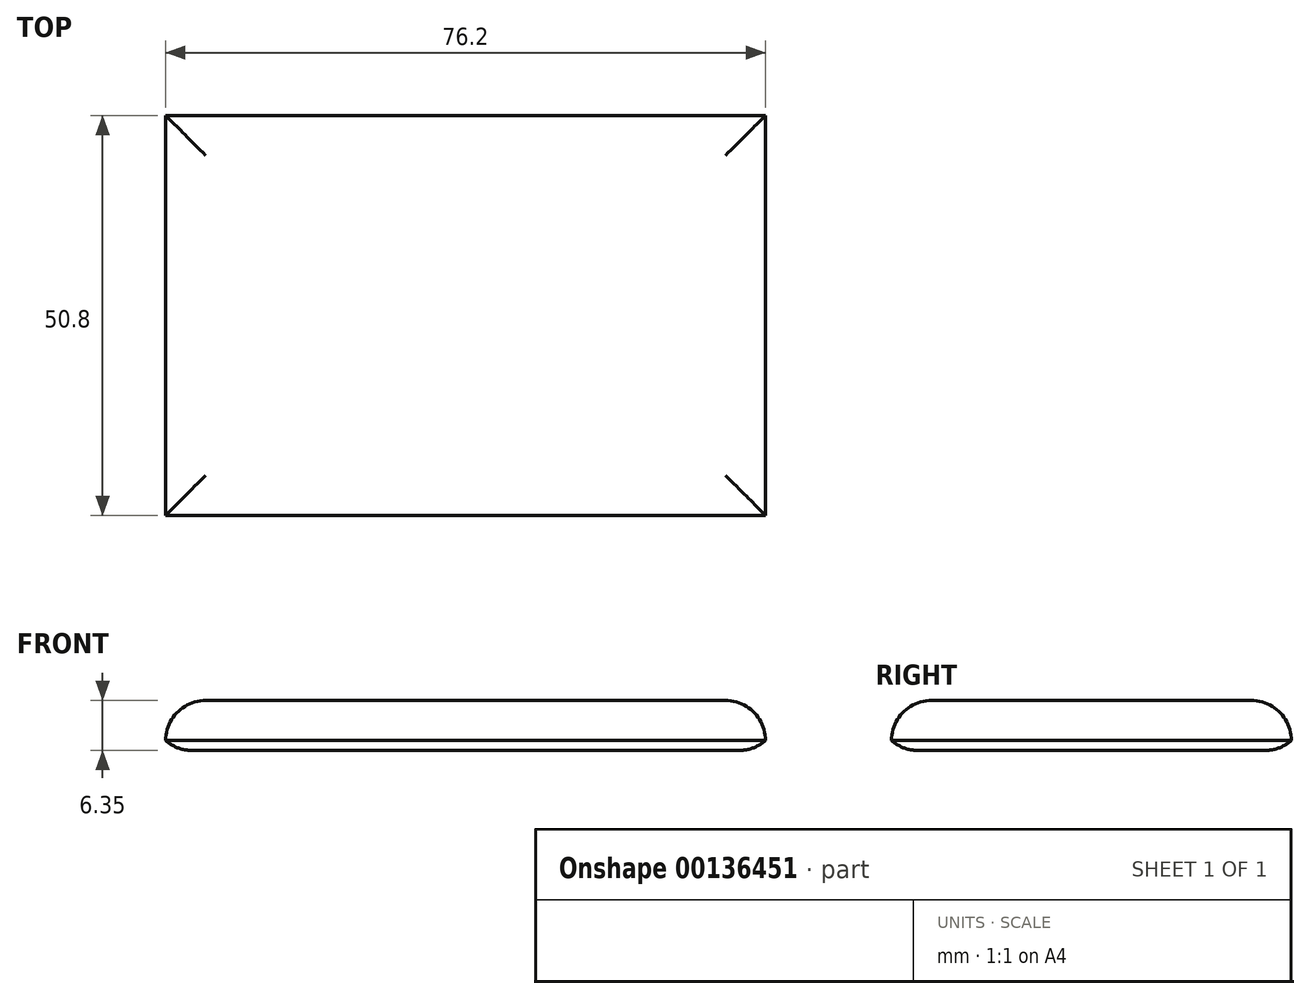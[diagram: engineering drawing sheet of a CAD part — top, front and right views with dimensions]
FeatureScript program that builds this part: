
annotation { "Feature Type Name" : "Feature", "Feature Type Description" : "" }
export const myFeature = defineFeature(function(context is Context, id is Id, definition is map)
    precondition{}
    {
        {
            var Q0;
            Q0=qCreatedBy(makeId("Top.planeOp"),FACE);
            var sketch = newSketch(context, id + "F0", { "sketchPlane" : qUnion([Q0])});
            skLineSegment(sketch, "E0.bottom", {"start": v(0, 0) * mm, "end": v(76.2, 0) * mm});
            skLineSegment(sketch, "E0.top", {"start": v(0, -50.8) * mm, "end": v(76.2, -50.8) * mm});
            skLineSegment(sketch, "E0.left", {"start": v(0, 0) * mm, "end": v(0, -50.8) * mm});
            skLineSegment(sketch, "E0.right", {"start": v(76.2, 0) * mm, "end": v(76.2, -50.8) * mm});
            skSolve(sketch);
        }
        {
            var Q0;
            Q0 = qSketchRegion(id + "F0", true);
            extrude(context, id + "F1", {"entities" : qUnion([Q0]), "depth" : 6.35 * mm});
        }
        {
            var Q0;
            Q0=makeQuery(id+"F1.opExtrude","CAP_FACE",FACE,{"disambiguationData":[OSD([sQuery(id+"F0.wireOp",EDGE,"E0.bottom"),sQuery(id+"F0.wireOp",EDGE,"E0.top"),sQuery(id+"F0.wireOp",EDGE,"E0.left"),sQuery(id+"F0.wireOp",EDGE,"E0.right")])],"isStart":false});
            fillet(context, id + "F2", {"entities" : qUnion([Q0]), "radius" : 5.08 * mm, "tangentPropagation" : true, "allowEdgeOverflow" : false});
        }
        {
            var Q0;
            Q0=makeQuery(id+"F1.opExtrude","CAP_FACE",FACE,{"disambiguationData":[OSD([sQuery(id+"F0.wireOp",EDGE,"E0.bottom"),sQuery(id+"F0.wireOp",EDGE,"E0.top"),sQuery(id+"F0.wireOp",EDGE,"E0.left"),sQuery(id+"F0.wireOp",EDGE,"E0.right")])],"isStart":true});
            fillet(context, id + "F3", {"entities" : qUnion([Q0]), "radius" : 5.08 * mm, "tangentPropagation" : true, "rho" : 0.5, "crossSection" : FilletCrossSection.CONIC, "allowEdgeOverflow" : false});
        }
    });
